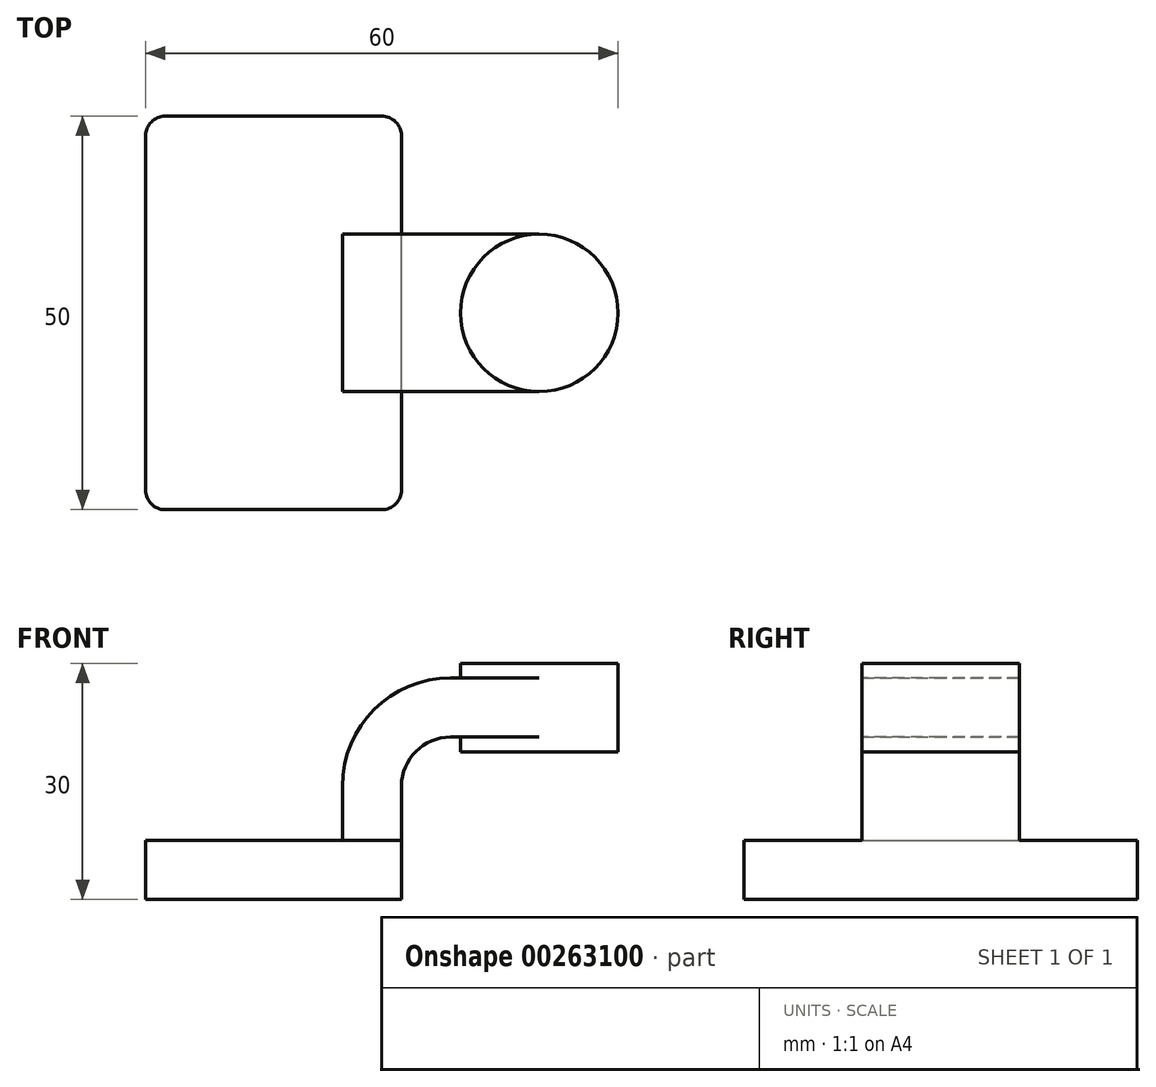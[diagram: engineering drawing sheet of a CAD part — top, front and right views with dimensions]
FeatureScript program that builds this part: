
annotation { "Feature Type Name" : "Feature", "Feature Type Description" : "" }
export const myFeature = defineFeature(function(context is Context, id is Id, definition is map)
    precondition{}
    {
        {
            var Q0;
            Q0=qCreatedBy(makeId("Front.planeOp"),FACE);
            var sketch = newSketch(context, id + "F0", { "sketchPlane" : qUnion([Q0])});
            skLineSegment(sketch, "E0.bottom", {"start": v(-16.25, -3.75) * mm, "end": v(16.25, -3.75) * mm});
            skLineSegment(sketch, "E0.top", {"start": v(-16.25, 3.75) * mm, "end": v(16.25, 3.75) * mm});
            skLineSegment(sketch, "E0.left", {"start": v(-16.25, -3.75) * mm, "end": v(-16.25, 3.75) * mm});
            skLineSegment(sketch, "E0.right", {"start": v(16.25, -3.75) * mm, "end": v(16.25, 3.75) * mm});
            skPoint(sketch, "E0.middle", {"position": v(0, 0) * mm});
            skLineSegment(sketch, "E1.bottom", {"start": v(23.75, 26.25) * mm, "end": v(43.75, 26.25) * mm});
            skLineSegment(sketch, "E1.top", {"start": v(23.75, 15) * mm, "end": v(43.75, 15) * mm});
            skLineSegment(sketch, "E1.left", {"start": v(23.75, 26.25) * mm, "end": v(23.75, 15) * mm});
            skLineSegment(sketch, "E1.right", {"start": v(43.75, 26.25) * mm, "end": v(43.75, 15) * mm});
            skPoint(sketch, "E1.middle", {"position": v(33.75, 20.63) * mm});
            skLineSegment(sketch, "E2", {"start": v(16.25, 3.75) * mm, "end": v(16.25, 10.63) * mm});
            skArc(sketch, "E3", {"start": v(16.25, 10.63) * mm, "mid": v(18.08, 15.05) * mm, "end": v(22.5, 16.88) * mm});
            skLineSegment(sketch, "E4", {"start": v(22.5, 16.88) * mm, "end": v(33.75, 16.88) * mm});
            skLineSegment(sketch, "E5.0", {"start": v(22.5, 24.38) * mm, "end": v(33.75, 24.38) * mm});
            skArc(sketch, "E5.1", {"start": v(8.75, 10.63) * mm, "mid": v(12.78, 20.35) * mm, "end": v(22.5, 24.38) * mm});
            skLineSegment(sketch, "E5.2", {"start": v(8.75, 3.75) * mm, "end": v(8.75, 10.63) * mm});
            skLineSegment(sketch, "E6", {"start": v(33.75, 15) * mm, "end": v(33.75, 26.25) * mm});
            skFitSpline(sketch, "E7", {"points": [v(-16.25, 3.75) * mm, v(22.5, 24.38) * mm], "startDerivative": vector(0, 37.02) * mm, "endDerivative": vector(46.88, 0) * mm});
            skSolve(sketch);
        }
        {
            var Q0;
            Q0=makeQuery(id+"F0.imprint","IMPRINT",FACE,{"disambiguationData":[TD([[makeQuery(id+"F0.imprint","IMPRINT",EDGE,{"derivedFrom":sQuery(id+"F0.wireOp",EDGE,"E0.bottom")}),1.0]])]});
            extrude(context, id + "F1", {"entities" : qUnion([Q0]), "endBound" : BoundingType.SYMMETRIC, "depth" : 50 * mm});
        }
        {
            var Q0;
            {var subQ1=sQuery(id+"F0.wireOp",EDGE,"E2");Q0=makeQuery(id+"F0.imprint","IMPRINT",FACE,{"disambiguationData":[TD([[makeQuery(id+"F0.imprint","IMPRINT",EDGE,{"derivedFrom":subQ1}),1.0]])]});}
            var Q1;
            {var subQ0=sQuery(id+"F0.wireOp",EDGE,"E5.0");var subQ1=sQuery(id+"F0.wireOp",EDGE,"E1.left");var subQ2=makeQuery(id+"F0.imprint","INTERSECT",VERTEX,{"derivedFrom":[subQ1,subQ0]});Q1=makeQuery(id+"F0.imprint","IMPRINT",FACE,{"disambiguationData":[TD([[makeQuery(id+"F0.imprint","IMPRINT",EDGE,{"disambiguationData":[TD([[subQ2,-1.0]])],"derivedFrom":subQ1}),1.0]])]});}
            extrude(context, id + "F2", {"entities" : qUnion([Q0, Q1]), "operationType" : NewBodyOperationType.ADD, "endBound" : BoundingType.SYMMETRIC, "depth" : 20 * mm});
        }
        {
            var Q0;
            Q0=makeQuery(id+"F0.imprint","IMPRINT",FACE,{"disambiguationData":[TD([[makeQuery(id+"F0.imprint","IMPRINT",EDGE,{"derivedFrom":sQuery(id+"F0.wireOp",EDGE,"E5.1")}),1.0]])]});
            extrude(context, id + "F3", {"entities" : qUnion([Q0]), "operationType" : NewBodyOperationType.ADD, "endBound" : BoundingType.SYMMETRIC, "depth" : 6.25 * mm});
        }
        {
            var Q0;
            {var subQ0=sQuery(id+"F0.wireOp",EDGE,"E1.right");Q0=makeQuery(id+"F0.imprint","IMPRINT",FACE,{"disambiguationData":[TD([[makeQuery(id+"F0.imprint","IMPRINT",EDGE,{"derivedFrom":subQ0}),-1.0]])]});}
            var Q1;
            Q1=sQuery(id+"F0.wireOp",EDGE,"E6");
            revolve(context, id + "F4", {"operationType" : NewBodyOperationType.ADD, "entities" : qUnion([Q0]), "axis" : qUnion([Q1]), "revolveType" : RevolveType.FULL});
        }
        {
            var Q0;
            Q0=makeQuery(id+"F1.opExtrude","CAP_EDGE",EDGE,{"disambiguationData":[OSD([sQuery(id+"F0.wireOp",EDGE,"E0.right")])],"isStart":false});
            var Q1;
            Q1=makeQuery(id+"F1.opExtrude","CAP_EDGE",EDGE,{"disambiguationData":[OSD([sQuery(id+"F0.wireOp",EDGE,"E0.right")])],"isStart":true});
            var Q2;
            Q2=makeQuery(id+"F1.opExtrude","CAP_EDGE",EDGE,{"disambiguationData":[OSD([sQuery(id+"F0.wireOp",EDGE,"E0.left")])],"isStart":true});
            var Q3;
            Q3=makeQuery(id+"F1.opExtrude","CAP_EDGE",EDGE,{"disambiguationData":[OSD([sQuery(id+"F0.wireOp",EDGE,"E0.left")])],"isStart":false});
            fillet(context, id + "F5", {"entities" : qUnion([Q0, Q1, Q2, Q3]), "radius" : 2.5 * mm, "tangentPropagation" : true, "allowEdgeOverflow" : false});
        }
    });
